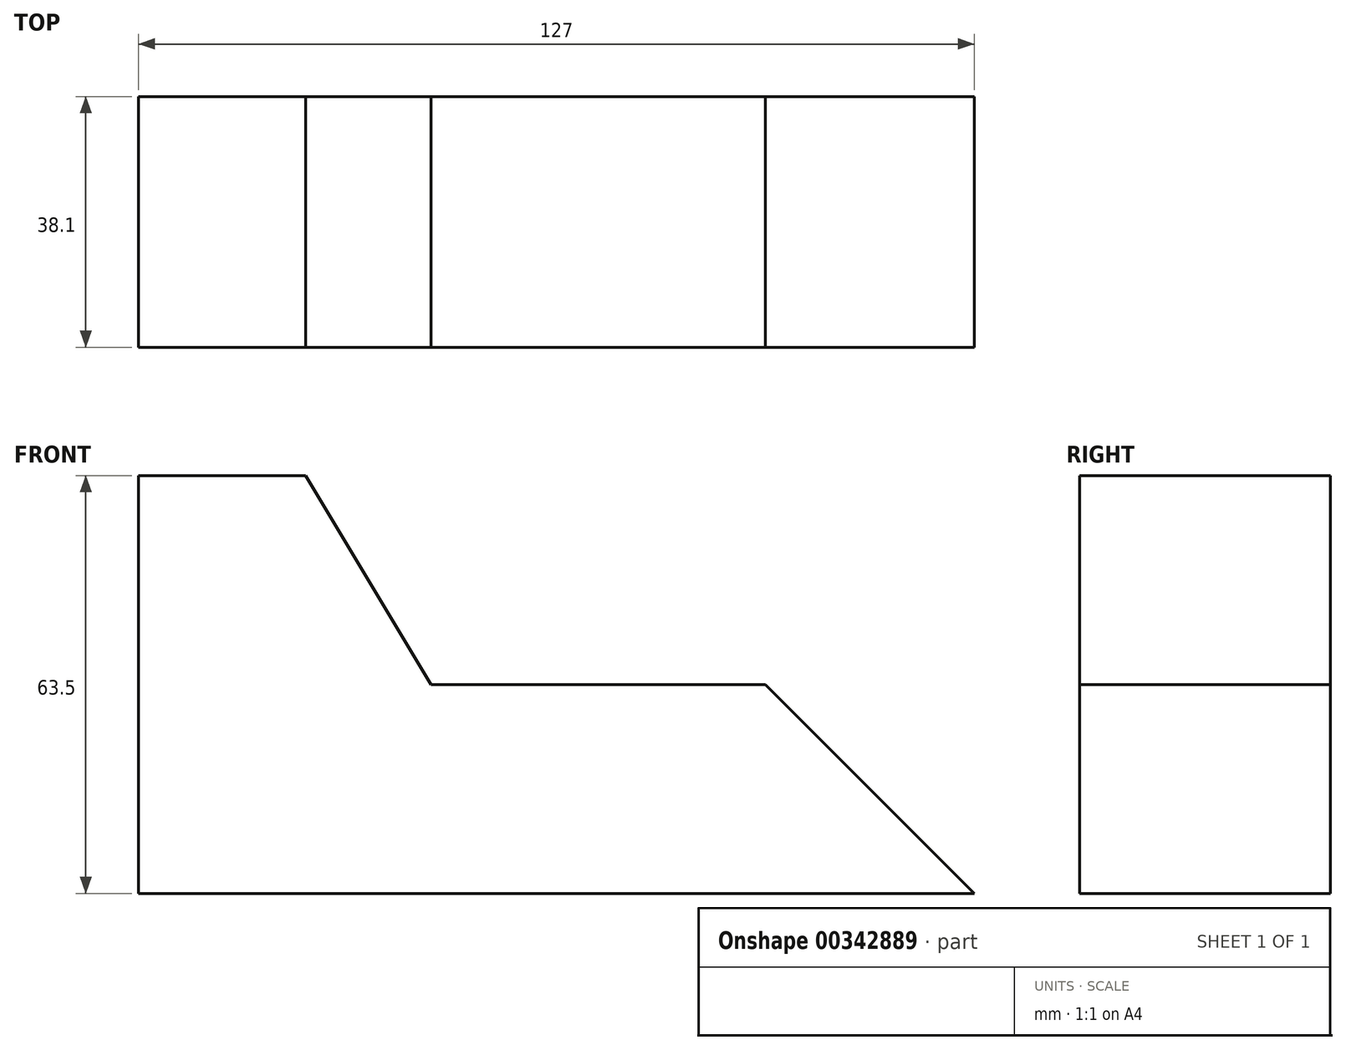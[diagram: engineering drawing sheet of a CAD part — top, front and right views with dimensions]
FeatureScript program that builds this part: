
annotation { "Feature Type Name" : "Feature", "Feature Type Description" : "" }
export const myFeature = defineFeature(function(context is Context, id is Id, definition is map)
    precondition{}
    {
        {
            var Q0;
            Q0=qCreatedBy(makeId("Front.planeOp"),FACE);
            var sketch = newSketch(context, id + "F0", { "sketchPlane" : qUnion([Q0])});
            skLineSegment(sketch, "E0", {"start": v(-38.72, -45.03) * mm, "end": v(88.28, -45.03) * mm});
            skLineSegment(sketch, "E1", {"start": v(-38.72, -45.03) * mm, "end": v(-38.72, 18.47) * mm});
            skLineSegment(sketch, "E2", {"start": v(-38.72, 18.47) * mm, "end": v(-13.32, 18.47) * mm});
            skLineSegment(sketch, "E3", {"start": v(-13.32, 18.47) * mm, "end": v(5.73, -13.28) * mm});
            skPoint(sketch, "E3.endSnap0", {"position": v(-38.72, -13.28) * mm});
            skLineSegment(sketch, "E4", {"start": v(5.73, -13.28) * mm, "end": v(56.53, -13.28) * mm});
            skLineSegment(sketch, "E5", {"start": v(56.53, -13.28) * mm, "end": v(88.28, -45.03) * mm});
            skPoint(sketch, "E6.end.orphan", {"position": v(5.73, 18.47) * mm});
            skSolve(sketch);
        }
        {
            var Q0;
            Q0=makeQuery(id+"F0.imprint","IMPRINT",FACE,{"disambiguationData":[TD([[makeQuery(id+"F0.imprint","IMPRINT",EDGE,{"derivedFrom":sQuery(id+"F0.wireOp",EDGE,"E0")}),1.0]])]});
            extrude(context, id + "F1", {"entities" : qUnion([Q0]), "depth" : 38.1 * mm});
        }
    });
